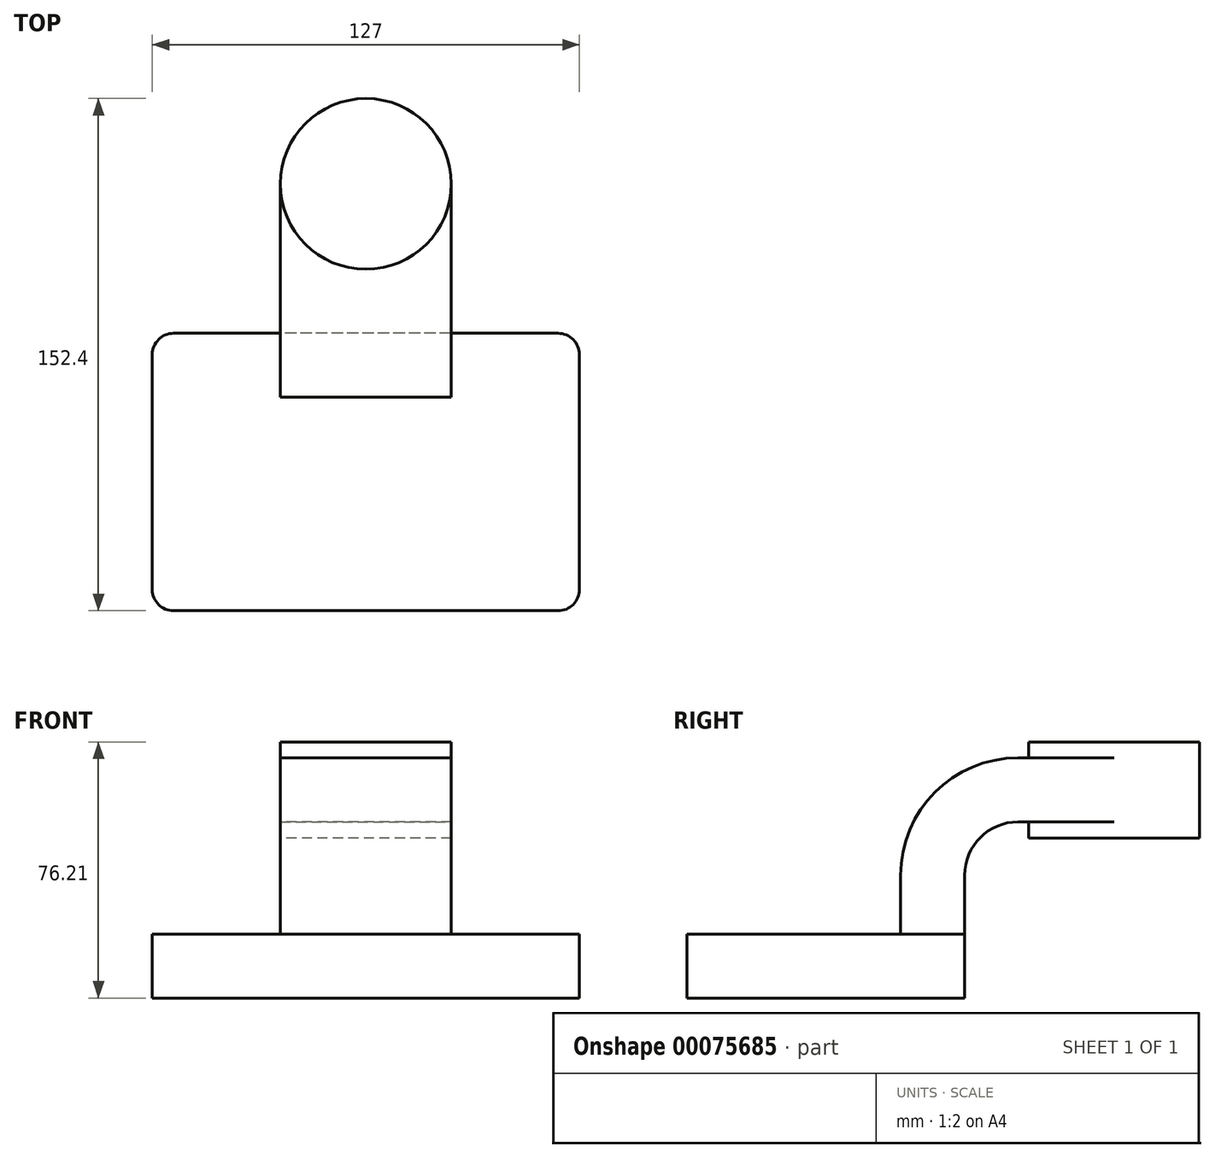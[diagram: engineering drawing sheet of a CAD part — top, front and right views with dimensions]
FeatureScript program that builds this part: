
annotation { "Feature Type Name" : "Feature", "Feature Type Description" : "" }
export const myFeature = defineFeature(function(context is Context, id is Id, definition is map)
    precondition{}
    {
        {
            var Q0;
            Q0=qCreatedBy(makeId("Right.planeOp"),FACE);
            var sketch = newSketch(context, id + "F0", { "sketchPlane" : qUnion([Q0])});
            skLineSegment(sketch, "E0.rect.bottom", {"start": v(41.28, -9.53) * mm, "end": v(-41.28, -9.53) * mm});
            skLineSegment(sketch, "E0.rect.top", {"start": v(41.27, 9.53) * mm, "end": v(-41.28, 9.53) * mm});
            skLineSegment(sketch, "E0.rect.left", {"start": v(41.28, -9.52) * mm, "end": v(41.28, 9.53) * mm});
            skLineSegment(sketch, "E0.rect.right", {"start": v(-41.28, -9.53) * mm, "end": v(-41.28, 9.53) * mm});
            skPoint(sketch, "E0.rect.middle", {"position": v(0, 0) * mm});
            skLineSegment(sketch, "E1.rect.bottom", {"start": v(111.12, 38.1) * mm, "end": v(60.33, 38.1) * mm});
            skLineSegment(sketch, "E1.rect.top", {"start": v(111.12, 66.67) * mm, "end": v(60.33, 66.67) * mm});
            skLineSegment(sketch, "E1.rect.left", {"start": v(111.13, 38.1) * mm, "end": v(111.13, 66.68) * mm});
            skLineSegment(sketch, "E1.rect.right", {"start": v(60.33, 38.1) * mm, "end": v(60.33, 66.68) * mm});
            skPoint(sketch, "E1.rect.middle", {"position": v(85.72, 52.39) * mm});
            skLineSegment(sketch, "E2", {"start": v(41.28, 9.53) * mm, "end": v(41.28, 27) * mm});
            skArc(sketch, "E3", {"start": v(41.28, 27) * mm, "mid": v(45.92, 38.23) * mm, "end": v(57.15, 42.88) * mm});
            skLineSegment(sketch, "E4", {"start": v(57.15, 42.88) * mm, "end": v(85.72, 42.88) * mm});
            skLineSegment(sketch, "E5.0", {"start": v(57.15, 61.93) * mm, "end": v(85.72, 61.93) * mm});
            skArc(sketch, "E5.1", {"start": v(22.23, 27) * mm, "mid": v(32.45, 51.7) * mm, "end": v(57.15, 61.93) * mm});
            skLineSegment(sketch, "E5.2", {"start": v(22.23, 8.4) * mm, "end": v(22.23, 27) * mm});
            skLineSegment(sketch, "E6", {"start": v(85.73, 66.68) * mm, "end": v(85.73, 38.1) * mm});
            skFitSpline(sketch, "E7", {"points": [v(57.15, 61.93) * mm, v(-41.28, 9.52) * mm], "startDerivative": vector(-109.08, 0) * mm, "endDerivative": vector(0, -115.55) * mm});
            skSolve(sketch);
        }
        {
            var Q0;
            Q0=makeQuery(id+"F0.imprint","IMPRINT",FACE,{"disambiguationData":[TD([[makeQuery(id+"F0.imprint","IMPRINT",EDGE,{"derivedFrom":sQuery(id+"F0.wireOp",EDGE,"E0.rect.bottom")}),-1.0]])]});
            extrude(context, id + "F1", {"entities" : qUnion([Q0]), "endBound" : BoundingType.SYMMETRIC, "depth" : 127 * mm});
        }
        {
            var Q0;
            {var subQ1=sQuery(id+"F0.wireOp",EDGE,"E2");Q0=makeQuery(id+"F0.imprint","IMPRINT",FACE,{"disambiguationData":[TD([[makeQuery(id+"F0.imprint","IMPRINT",EDGE,{"derivedFrom":subQ1}),1.0]])]});}
            var Q1;
            {var subQ0=sQuery(id+"F0.wireOp",EDGE,"E4");var subQ1=sQuery(id+"F0.wireOp",EDGE,"E1.rect.right");var subQ2=makeQuery(id+"F0.imprint","INTERSECT",VERTEX,{"derivedFrom":[subQ1,subQ0]});Q1=makeQuery(id+"F0.imprint","IMPRINT",FACE,{"disambiguationData":[TD([[makeQuery(id+"F0.imprint","IMPRINT",EDGE,{"disambiguationData":[TD([[subQ2,-1.0]])],"derivedFrom":subQ1}),-1.0]])]});}
            extrude(context, id + "F2", {"entities" : qUnion([Q0, Q1]), "operationType" : NewBodyOperationType.ADD, "endBound" : BoundingType.SYMMETRIC, "depth" : 50.8 * mm});
        }
        {
            var Q0;
            {var subQ4=sQuery(id+"F0.wireOp",EDGE,"E5.1");Q0=makeQuery(id+"F0.imprint","IMPRINT",FACE,{"disambiguationData":[TD([[makeQuery(id+"F0.imprint","IMPRINT",EDGE,{"derivedFrom":subQ4}),1.0]])]});}
            extrude(context, id + "F3", {"entities" : qUnion([Q0]), "operationType" : NewBodyOperationType.ADD, "endBound" : BoundingType.SYMMETRIC, "depth" : 15.88 * mm});
        }
        {
            var Q0;
            {var subQ0=sQuery(id+"F0.wireOp",EDGE,"E1.rect.left");Q0=makeQuery(id+"F0.imprint","IMPRINT",FACE,{"disambiguationData":[TD([[makeQuery(id+"F0.imprint","IMPRINT",EDGE,{"derivedFrom":subQ0}),1.0]])]});}
            var Q1;
            Q1=sQuery(id+"F0.wireOp",EDGE,"E6");
            revolve(context, id + "F4", {"operationType" : NewBodyOperationType.ADD, "entities" : qUnion([Q0]), "axis" : qUnion([Q1]), "revolveType" : RevolveType.FULL});
        }
        {
            var Q0;
            Q0=makeQuery(id+"F1.opExtrude","CAP_EDGE",EDGE,{"disambiguationData":[OSD([sQuery(id+"F0.wireOp",EDGE,"E0.rect.left")])],"isStart":false});
            var Q1;
            Q1=makeQuery(id+"F1.opExtrude","CAP_EDGE",EDGE,{"disambiguationData":[OSD([sQuery(id+"F0.wireOp",EDGE,"E0.rect.right")])],"isStart":false});
            var Q2;
            Q2=makeQuery(id+"F1.opExtrude","CAP_EDGE",EDGE,{"disambiguationData":[OSD([sQuery(id+"F0.wireOp",EDGE,"E0.rect.right")])],"isStart":true});
            var Q3;
            Q3=makeQuery(id+"F1.opExtrude","CAP_EDGE",EDGE,{"disambiguationData":[OSD([sQuery(id+"F0.wireOp",EDGE,"E0.rect.left")])],"isStart":true});
            fillet(context, id + "F5", {"entities" : qUnion([Q0, Q1, Q2, Q3]), "radius" : 6.35 * mm, "tangentPropagation" : true, "allowEdgeOverflow" : false});
        }
    });
